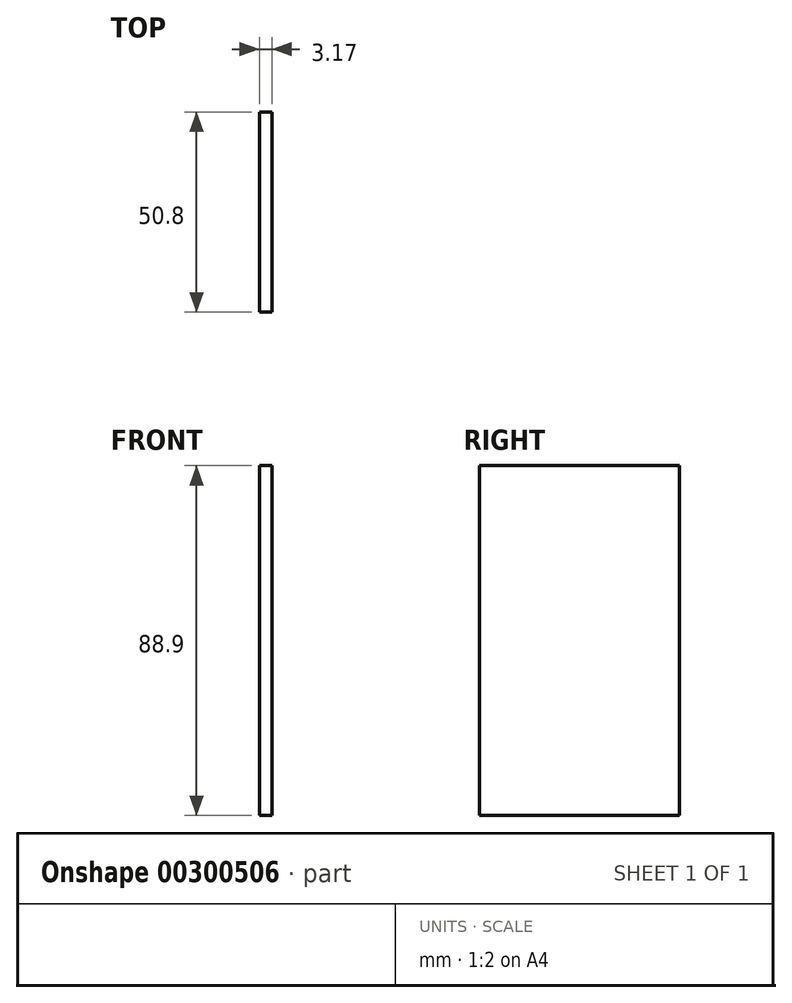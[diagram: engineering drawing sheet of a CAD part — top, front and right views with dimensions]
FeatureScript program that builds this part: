
annotation { "Feature Type Name" : "Feature", "Feature Type Description" : "" }
export const myFeature = defineFeature(function(context is Context, id is Id, definition is map)
    precondition{}
    {
        {
            var Q0;
            Q0=qCreatedBy(makeId("Right.planeOp"),FACE);
            var sketch = newSketch(context, id + "F0", { "sketchPlane" : qUnion([Q0])});
            skLineSegment(sketch, "E0.bottom", {"start": v(-39.39, 49.98) * mm, "end": v(11.41, 49.98) * mm});
            skLineSegment(sketch, "E0.top", {"start": v(-39.39, -38.92) * mm, "end": v(11.41, -38.92) * mm});
            skLineSegment(sketch, "E0.left", {"start": v(-39.39, 49.98) * mm, "end": v(-39.39, -38.92) * mm});
            skLineSegment(sketch, "E0.right", {"start": v(11.41, 49.98) * mm, "end": v(11.41, -38.92) * mm});
            skSolve(sketch);
        }
        {
            var Q0;
            Q0 = qSketchRegion(id + "F0", true);
            extrude(context, id + "F1", {"entities" : qUnion([Q0]), "depth" : 3.17 * mm});
        }
    });
